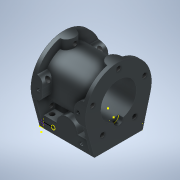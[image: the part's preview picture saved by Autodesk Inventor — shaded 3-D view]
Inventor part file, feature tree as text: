
AUTODESK INVENTOR PART (.ipt)
format: ipt  version: 2020 (Build 240168000, 168)  size: 633,344 bytes
history: native  units: mm
features: sketch x38, extrude x20, thread x14, other x9, hole x6, plane x6, fillet x4, projected_geometry x2
ambient origin geometry x8: Origin, YZ Plane, XZ Plane, XY Plane, X Axis, Y Axis, Z Axis, Center Point
bodies: Solid1 (feature_tree)
feature tree (99):
  sketch  "Sketch1"  dims[d0=35.0mm d1=25.5mm]
  sketch  "Sketch2"  dims[d2=12.75mm d3=2.0mm d4=0.0mm]
  extrude  "Extrusion1"  Depth=25.5mm
  extrude  "Extrusion2"  Depth=2.0mm TaperAngle=0.0deg
  extrude  "Extrusion3"  Depth=13.5mm
  extrude  "Extrusion4"  Depth=6.0mm
  extrude  "Extrusion5"  Depth=6.0mm
  extrude  "Extrusion6"  TaperAngle=90.0deg  [1 undecoded]
  fillet  "Fillet1"  Radius=25.0mm
  extrude  "Extrusion7"  Depth=2.0mm TaperAngle=0.0deg
  fillet  "Fillet2"  Radius=5.5mm
  hole  "Hole1"  [1 undecoded]
  thread  "Thread1"  [1 undecoded]
  thread  "Thread2"  [1 undecoded]
  thread  "Thread3"  [1 undecoded]
  thread  "Thread4"  [1 undecoded]
  extrude  "Extrusion8"  Depth=2.0mm
  extrude  "Extrusion9"  Depth=9.25mm
  extrude  "Extrusion10"  Depth=20.0mm
  sketch  "Sketch14"  dims[d37=8.0mm d38=4.0mm d39=0.0mm]
  sketch  "Sketch15"  dims[d40=4.0mm d41=4.0mm]
  plane  "Work Plane1"
  extrude  "Extrusion11"  Depth=9.25mm
  other  "UCS1"
  other  "Work Point1"
  sketch  "Sketch19"  dims[d45=4.0mm d46=2.75mm]
  plane  "Work Plane2"
  sketch  "Sketch20"  dims[d47=3.75mm d48=20.0mm]
  hole  "Hole3"  [1 undecoded]
  sketch  "Sketch24"  dims[d51=3.75mm d52=2.75mm d53=3.75mm]
  sketch  "Sketch25"  dims[d54=2.5mm d55=6.0mm d56=4.0mm d57=2.0mm d58=90.0deg d59=7.0mm d60=20.594885mm d61=6.0mm d62=0.0mm d63=6.0mm d64=0.0mm d65=6.0mm d66=0.0mm d67=6.0mm d68=0.0mm d69=19.0mm d70=0.0mm d71=0.0mm d72=2.5mm d73=5.0mm d74=2.5mm]
  plane  "Work Plane3"
  hole  "Hole4"  [1 undecoded]
  extrude  "Extrusion14"  Depth=4.0mm
  sketch  "Sketch28"  dims[d82=2.0mm d83=9.0mm d84=4.0mm d85=0.0mm d86=0.0mm]
  sketch  "Sketch29"  dims[d87=0.0mm d88=0.0mm d89=0.0mm d90=0.0mm d91=0.0mm d92=-5.235988mm d94=300.0deg]
  plane  "Work Plane4"
  hole  "Hole5"  [1 undecoded]
  extrude  "Extrusion15"  Depth=2.75mm
  extrude  "Extrusion16"  Depth=20.0mm
  extrude  "Extrusion17"  Depth=20.0mm
  extrude  "Extrusion18"  Depth=2.75mm
  thread  "Thread5"  [1 undecoded]
  thread  "Thread6"  [1 undecoded]
  thread  "Thread7"  [1 undecoded]
  thread  "Thread8"  [1 undecoded]
  thread  "Thread9"  [1 undecoded]
  thread  "Thread10"  [1 undecoded]
  thread  "Thread11"  [1 undecoded]
  thread  "Thread12"  [1 undecoded]
  thread  "Thread13"  [1 undecoded]
  thread  "Thread14"  [1 undecoded]
  extrude  "Extrusion19"  Depth=2.5mm
  extrude  "Extrusion20"  Depth=2.5mm TaperAngle=0.0deg
  fillet  "Fillet4"  [1 undecoded]
  extrude  "Extrusion21"  Depth=9.0mm TaperAngle=0.0deg
  extrude  "Extrusion22"  TaperAngle=300.0deg  [1 undecoded]
  fillet  "Fillet5"  Radius=3.0mm
  sketch  "Sketch39"  dims[d140=1.0mm d141=0.0mm]
  plane  "Work Plane5"
  hole  "Hole6"  [1 undecoded]
  sketch  "Sketch41"  dims[d143=9.0mm d144=4.0mm d145=0.0mm d146=0.0mm]
  plane  "Work Plane6"
  hole  "Hole7"  [1 undecoded]
  sketch  "Sketch3"  dims[d5=25.5mm d6=13.5mm]
  sketch  "Sketch4"  dims[d7=6.75mm d8=6.0mm]
  sketch  "Sketch5"  dims[d9=25.5mm d10=6.0mm]
  sketch  "Sketch6"  dims[d11=0.0mm d12=90.0deg d13=25.0mm d14=0.0mm]
  sketch  "Sketch7"  dims[d15=35.0mm d16=2.0mm d17=0.0mm d18=5.5mm]
  sketch  "Sketch8"  dims[d19=25.5mm d20=0.0mm d21=2.0mm d22=7.0mm d23=9.0mm d24=9.25mm d25=9.25mm]
  sketch  "Sketch9"  dims[d26=3.0mm d27=2.0mm]
  sketch  "Sketch10"  dims[d28=9.25mm d29=9.25mm]
  sketch  "Sketch11"  dims[d30=2.0mm d31=20.0mm]
  sketch  "Sketch12"  dims[d32=9.25mm d33=9.25mm]
  sketch  "Sketch13"  dims[d34=5.0mm d35=0.0mm d36=4.0mm]
  sketch  "Sketch16"  dims[d42=8.0mm d43=4.0mm d44=0.0mm]
  sketch  "Sketch23"  dims[d49=21.5mm d50=20.0mm]
  sketch  "Sketch26"  dims[d75=2.5mm d76=0.0mm d77=2.5mm]
  sketch  "Sketch27"  dims[d78=5.0mm d79=2.5mm d80=0.0mm d81=120.0deg]
  sketch  "Sketch30"  dims[d108=3.0mm d109=6.0mm d110=5.0mm d111=5.0mm d112=90.0deg d113=16.0mm d114=20.594885mm d115=3.0mm]
  sketch  "Sketch31"  dims[d116=180.0deg d118=7.0mm]
  sketch  "Sketch32"  dims[d119=7.0mm]
  sketch  "Sketch33"  dims[d120=2.0mm d121=6.0mm d122=5.0mm d123=5.0mm d124=90.0deg d125=7.0mm d126=20.594885mm d127=1.0mm d128=0.0mm]
  sketch  "Sketch34"  dims[d129=3.0mm]
  sketch  "Sketch35"  dims[d130=180.0deg]
  sketch  "Sketch36"  dims[d131=7.0mm]
  sketch  "Sketch37"  dims[d132=7.0mm]
  sketch  "Sketch38"  dims[d133=2.0mm d134=6.0mm d135=5.0mm d136=5.0mm d137=90.0deg d138=7.0mm d139=20.594885mm]
  sketch  "Sketch40"  dims[d142=2.0mm]
  projected_geometry  "Projected Loop1"
  projected_geometry  "Projected Loop2"
  sketch  "Sketch42"  dims[d147=2.5mm d148=14.5mm d149=50.0mm d151=360.0deg d153=6.0mm d154=0.0mm d155=50.0mm d157=360.0deg d159=6.0mm d160=0.0mm d161=6.0mm d162=0.0mm d163=2.0mm d164=0.0mm d165=2.0mm d166=0.0mm d167=2.0mm d168=0.0mm d169=2.0mm d170=0.0mm d171=2.0mm d172=0.0mm d173=2.0mm d174=0.0mm d175=2.0mm d176=0.0mm d177=2.0mm d178=0.0mm d179=6.0mm d180=0.0mm d181=11.0mm d182=11.0mm d183=4.0mm d184=0.0mm d186=11.0mm d187=11.0mm d188=4.0mm d189=0.0mm d190=4.0mm d191=4.0mm d192=0.0mm d193=4.0mm d194=0.0mm d195=4.0mm d196=1.5mm d197=1.5mm d198=4.0mm d199=5.5mm d200=5.5mm d201=4.0mm d202=2.0mm d203=6.0mm d204=4.0mm d205=2.0mm d206=90.0deg d207=5.0mm d208=20.594885mm d209=1.5mm d210=2.0mm d211=1.5mm d212=2.0mm d213=1.5mm d214=2.0mm d215=6.0mm d216=4.0mm d217=2.0mm d218=90.0deg d219=5.0mm d220=20.594885mm d95=1.0mm d96=1.0mm d97=0.15mm d98=0.25mm d99=0.375mm d100=14.3117mm d101=0.75mm d102=20.594885mm d103=0.0625mm d104=0.75mm d105=0.375mm]
  other  "UCS1: YZ Plane"
  other  "UCS1: XZ Plane"
  other  "UCS1: XY Plane"
  other  "UCS1: X Axis"
  other  "UCS1: Y Axis"
  other  "UCS1: Z Axis"
  other  "UCS1: Center Point"
note: 23 required parameter values undecoded (feature->parameter linkage not recoverable at this tier; creation-order binding heuristic only, values carry confidence <= 0.55)
